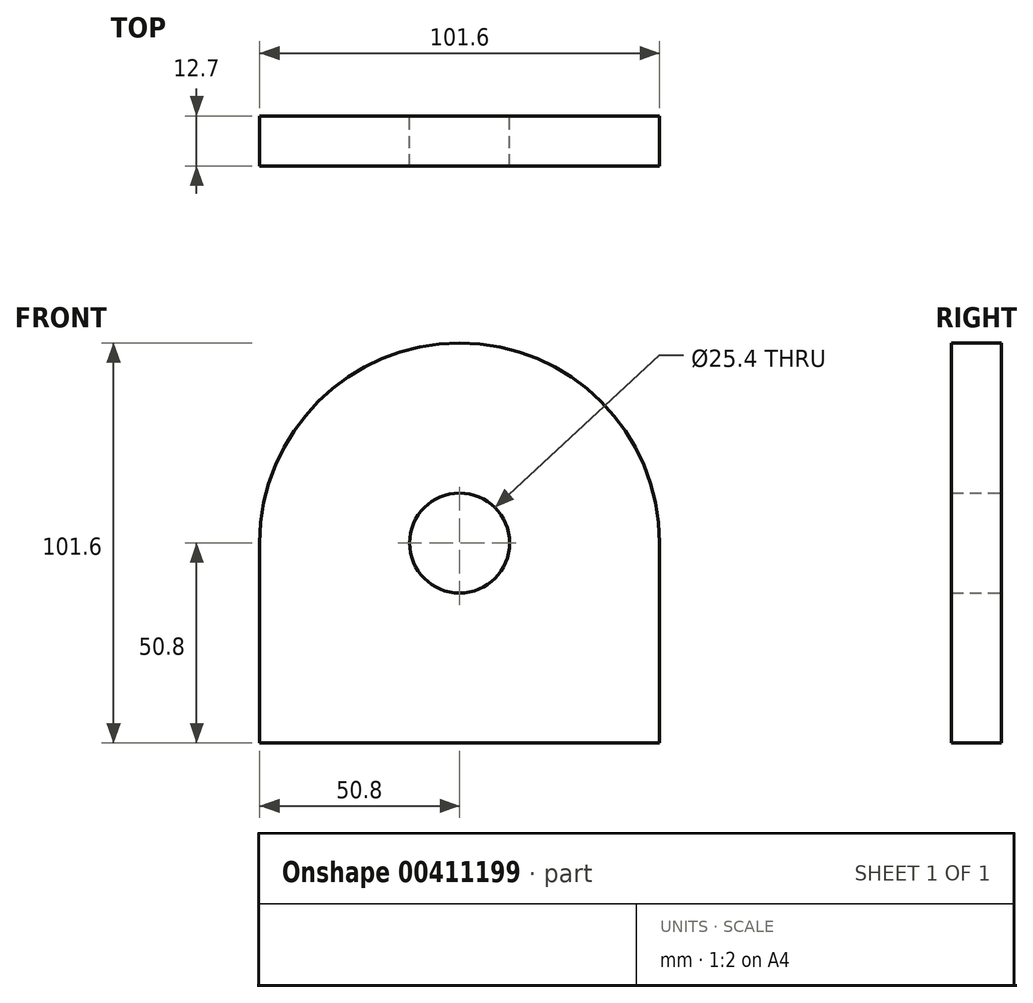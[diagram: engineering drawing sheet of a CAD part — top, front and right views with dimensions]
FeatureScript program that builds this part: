
annotation { "Feature Type Name" : "Feature", "Feature Type Description" : "" }
export const myFeature = defineFeature(function(context is Context, id is Id, definition is map)
    precondition{}
    {
        {
            var Q0;
            Q0=qCreatedBy(makeId("Front.planeOp"),FACE);
            var sketch = newSketch(context, id + "F0", { "sketchPlane" : qUnion([Q0])});
            skLineSegment(sketch, "E0", {"start": v(-50.8, 0) * mm, "end": v(-50.8, -50.8) * mm});
            skLineSegment(sketch, "E1", {"start": v(-50.8, -50.8) * mm, "end": v(50.8, -50.8) * mm});
            skLineSegment(sketch, "E2", {"start": v(50.8, -50.8) * mm, "end": v(50.8, 0) * mm});
            skArc(sketch, "E3", {"start": v(50.8, 0) * mm, "mid": v(0, 50.8) * mm, "end": v(-50.8, 0) * mm});
            skCircle(sketch, "E4", {"center": v(0, 0) * mm, "radius": 12.7 * mm});
            skSolve(sketch);
        }
        {
            var Q0;
            Q0=makeQuery(id+"F0.imprint","IMPRINT",FACE,{"disambiguationData":[TD([[makeQuery(id+"F0.imprint","IMPRINT",EDGE,{"derivedFrom":sQuery(id+"F0.wireOp",EDGE,"E0")}),1.0]])]});
            extrude(context, id + "F1", {"entities" : qUnion([Q0]), "depth" : 12.7 * mm});
        }
    });
